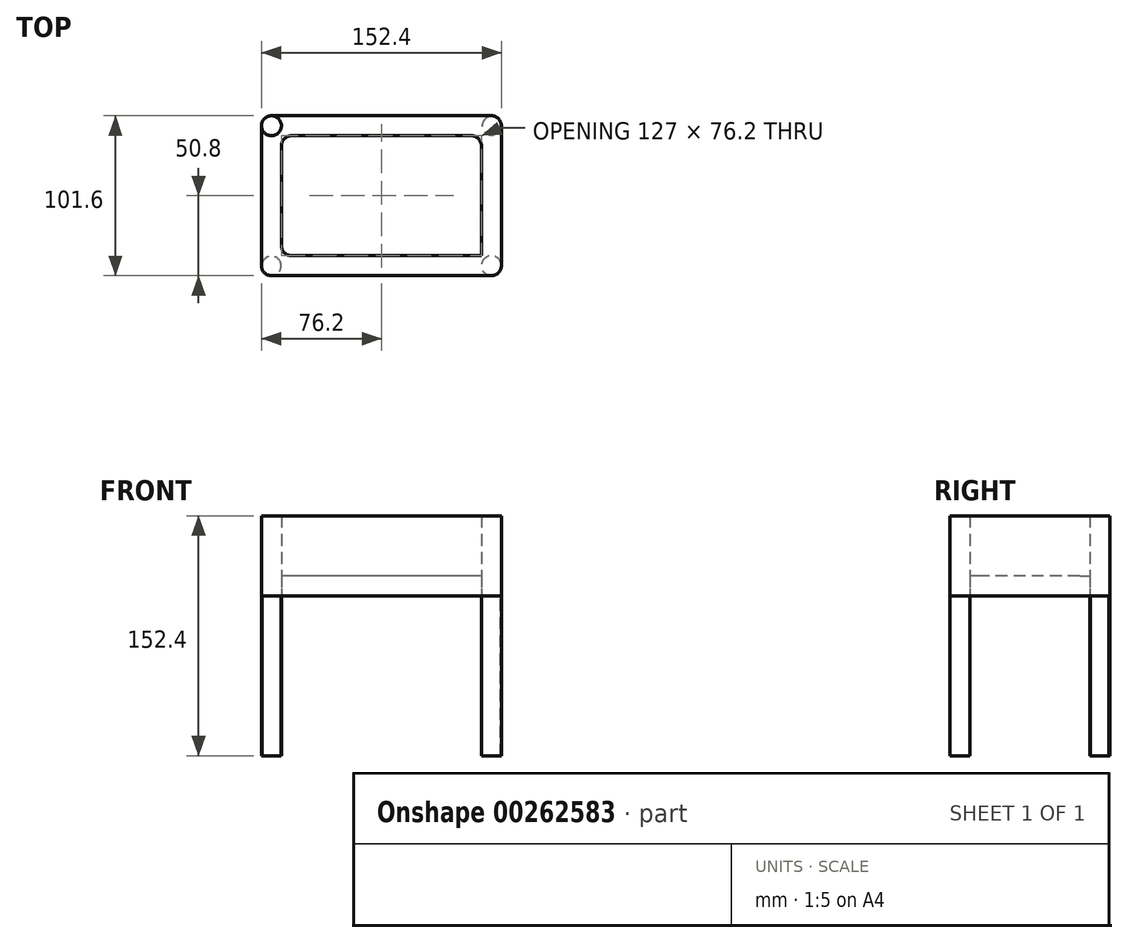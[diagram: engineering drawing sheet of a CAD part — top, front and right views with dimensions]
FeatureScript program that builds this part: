
annotation { "Feature Type Name" : "Feature", "Feature Type Description" : "" }
export const myFeature = defineFeature(function(context is Context, id is Id, definition is map)
    precondition{}
    {
        {
            var Q0;
            Q0=qCreatedBy(makeId("Top.planeOp"),FACE);
            var sketch = newSketch(context, id + "F0", { "sketchPlane" : qUnion([Q0])});
            skLineSegment(sketch, "E0.bottom", {"start": v(69.85, 50.8) * mm, "end": v(-69.85, 50.8) * mm});
            skLineSegment(sketch, "E0.top", {"start": v(69.85, -50.8) * mm, "end": v(-69.85, -50.8) * mm});
            skLineSegment(sketch, "E0.left", {"start": v(76.2, 44.45) * mm, "end": v(76.2, -44.45) * mm});
            skLineSegment(sketch, "E0.right", {"start": v(-76.2, 44.45) * mm, "end": v(-76.2, -44.45) * mm});
            skPoint(sketch, "E0.middle", {"position": v(0, 0) * mm});
            skLineSegment(sketch, "E1.bottom", {"start": v(57.15, 38.1) * mm, "end": v(-57.15, 38.1) * mm});
            skLineSegment(sketch, "E1.top", {"start": v(63.5, -38.1) * mm, "end": v(-57.15, -38.1) * mm});
            skLineSegment(sketch, "E1.left", {"start": v(63.5, 31.75) * mm, "end": v(63.5, -38.1) * mm});
            skLineSegment(sketch, "E1.right", {"start": v(-63.5, 31.75) * mm, "end": v(-63.5, -31.75) * mm});
            skPoint(sketch, "E2.visualSharp", {"position": v(-76.2, 50.8) * mm});
            skArc(sketch, "E2.filletArc", {"start": v(-69.85, 50.8) * mm, "mid": v(-74.34, 48.94) * mm, "end": v(-76.2, 44.45) * mm});
            skPoint(sketch, "E3.visualSharp", {"position": v(-63.5, 38.1) * mm});
            skArc(sketch, "E3.filletArc", {"start": v(-57.15, 38.1) * mm, "mid": v(-61.64, 36.24) * mm, "end": v(-63.5, 31.75) * mm});
            skPoint(sketch, "E4.visualSharp", {"position": v(76.2, 50.8) * mm});
            skArc(sketch, "E4.filletArc", {"start": v(76.2, 44.45) * mm, "mid": v(74.34, 48.94) * mm, "end": v(69.85, 50.8) * mm});
            skPoint(sketch, "E5.visualSharp", {"position": v(63.5, 38.1) * mm});
            skArc(sketch, "E5.filletArc", {"start": v(63.5, 31.75) * mm, "mid": v(61.64, 36.24) * mm, "end": v(57.15, 38.1) * mm});
            skPoint(sketch, "E6.visualSharp", {"position": v(76.2, -50.8) * mm});
            skArc(sketch, "E6.filletArc", {"start": v(69.85, -50.8) * mm, "mid": v(74.34, -48.94) * mm, "end": v(76.2, -44.45) * mm});
            skPoint(sketch, "E7.visualSharp", {"position": v(-76.2, -50.8) * mm});
            skArc(sketch, "E7.filletArc", {"start": v(-76.2, -44.45) * mm, "mid": v(-74.34, -48.94) * mm, "end": v(-69.85, -50.8) * mm});
            skPoint(sketch, "E8.visualSharp", {"position": v(-63.5, -38.1) * mm});
            skArc(sketch, "E8.filletArc", {"start": v(-63.5, -31.75) * mm, "mid": v(-61.64, -36.24) * mm, "end": v(-57.15, -38.1) * mm});
            skCircle(sketch, "E9", {"center": v(-69.85, 44.45) * mm, "radius": 6.35 * mm});
            skCircle(sketch, "E10", {"center": v(69.85, 44.45) * mm, "radius": 5.9 * mm});
            skCircle(sketch, "E11", {"center": v(69.85, -44.45) * mm, "radius": 6.35 * mm});
            skCircle(sketch, "E12", {"center": v(-69.85, -44.45) * mm, "radius": 6.11 * mm});
            skSolve(sketch);
        }
        {
            var Q0;
            Q0 = qSketchRegion(id + "F0", true);
            var Q1;
            Q1=makeQuery(id+"F0.imprint","IMPRINT",FACE,{"disambiguationData":[TD([[makeQuery(id+"F0.imprint","IMPRINT",EDGE,{"derivedFrom":sQuery(id+"F0.wireOp",EDGE,"E10")}),1.0]])]});
            var Q2;
            Q2=makeQuery(id+"F0.imprint","IMPRINT",FACE,{"disambiguationData":[TD([[makeQuery(id+"F0.imprint","IMPRINT",EDGE,{"derivedFrom":sQuery(id+"F0.wireOp",EDGE,"E12")}),1.0]])]});
            extrude(context, id + "F1", {"entities" : qUnion([Q0, Q1, Q2]), "depth" : 50.8 * mm});
        }
        {
            var Q0;
            {var subQ0=sQuery(id+"F0.wireOp",EDGE,"E9");var subQ1=makeQuery(id+"F0.imprint","INTERSECT",VERTEX,{"derivedFrom":[sQuery(id+"F0.wireOp",EDGE,"E0.bottom"),subQ0]});Q0=makeQuery(id+"F0.imprint","IMPRINT",FACE,{"disambiguationData":[TD([[makeQuery(id+"F0.imprint","IMPRINT",EDGE,{"disambiguationData":[TD([[subQ1,-1.0]])],"derivedFrom":subQ0}),1.0]])]});}
            var Q1;
            Q1=makeQuery(id+"F0.imprint","IMPRINT",FACE,{"disambiguationData":[TD([[makeQuery(id+"F0.imprint","IMPRINT",EDGE,{"derivedFrom":sQuery(id+"F0.wireOp",EDGE,"E10")}),1.0]])]});
            var Q2;
            {var subQ0=sQuery(id+"F0.wireOp",EDGE,"E11");var subQ1=makeQuery(id+"F0.imprint","INTERSECT",VERTEX,{"derivedFrom":[sQuery(id+"F0.wireOp",EDGE,"E0.top"),subQ0]});Q2=makeQuery(id+"F0.imprint","IMPRINT",FACE,{"disambiguationData":[TD([[makeQuery(id+"F0.imprint","IMPRINT",EDGE,{"disambiguationData":[TD([[subQ1,1.0]])],"derivedFrom":subQ0}),1.0]])]});}
            var Q3;
            Q3=makeQuery(id+"F0.imprint","IMPRINT",FACE,{"disambiguationData":[TD([[makeQuery(id+"F0.imprint","IMPRINT",EDGE,{"derivedFrom":sQuery(id+"F0.wireOp",EDGE,"E12")}),1.0]])]});
            extrude(context, id + "F2", {"entities" : qUnion([Q0, Q1, Q2, Q3]), "oppositeDirection" : true, "depth" : 101.6 * mm});
        }
        {
            var Q0;
            Q0=makeQuery(id+"F0.imprint","IMPRINT",FACE,{"disambiguationData":[TD([[makeQuery(id+"F0.imprint","IMPRINT",EDGE,{"derivedFrom":sQuery(id+"F0.wireOp",EDGE,"E1.bottom")}),1.0]])]});
            extrude(context, id + "F3", {"entities" : qUnion([Q0]), "depth" : 12.7 * mm});
        }
    });
